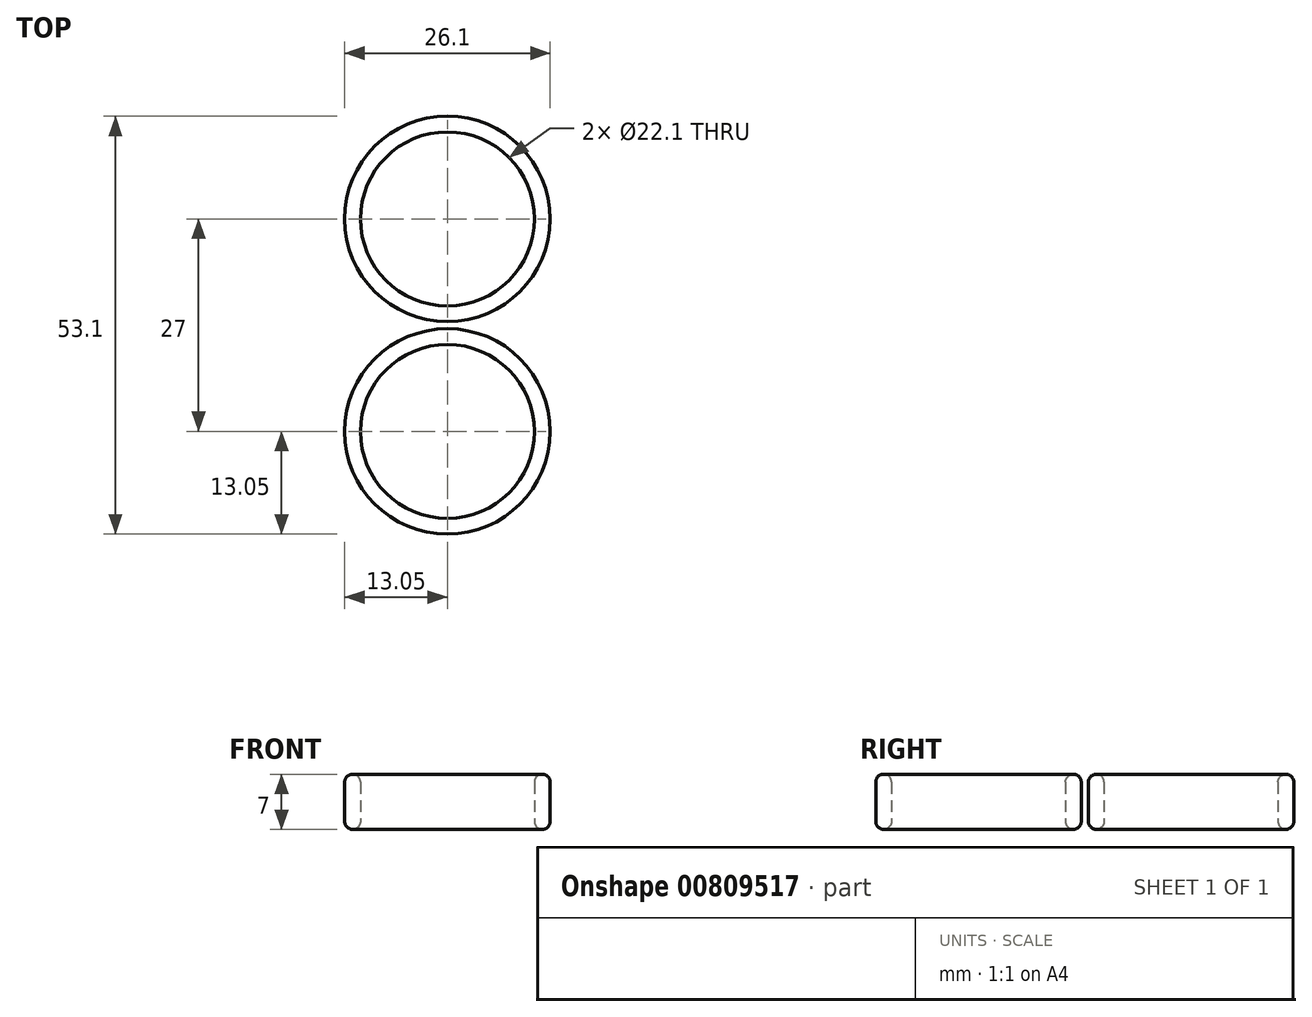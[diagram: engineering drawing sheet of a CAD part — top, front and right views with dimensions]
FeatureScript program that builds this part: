
annotation { "Feature Type Name" : "Feature", "Feature Type Description" : "" }
export const myFeature = defineFeature(function(context is Context, id is Id, definition is map)
    precondition{}
    {
        {
            var Q0;
            Q0=qCreatedBy(makeId("Top.planeOp"),FACE);
            var sketch = newSketch(context, id + "F0", { "sketchPlane" : qUnion([Q0])});
            skCircle(sketch, "E0", {"center": v(0, 0) * mm, "radius": 11.05 * mm});
            skCircle(sketch, "E1.0", {"center": v(0, 0) * mm, "radius": 13.05 * mm});
            skCircle(sketch, "E2", {"center": v(0, 27) * mm, "radius": 11.05 * mm});
            skCircle(sketch, "E3.0", {"center": v(0, 27) * mm, "radius": 13.05 * mm});
            skFitSpline(sketch, "E4", {"points": [v(12.68, 3.09) * mm, v(1.73, 13.5) * mm, v(12.68, 23.91) * mm], "startDerivative": vector(-13.43, 55.17) * mm, "endDerivative": vector(13.43, 55.17) * mm});
            skFitSpline(sketch, "E5", {"points": [v(-13.04, 27.4) * mm, v(-20.12, 13.5) * mm, v(-13.04, -0.4) * mm], "startDerivative": vector(-2.22, -73.4) * mm, "endDerivative": vector(2.22, -73.4) * mm});
            skLineSegment(sketch, "E6", {"start": v(0, 58.81) * mm, "end": v(0, -18.81) * mm, "construction": true});
            skLineSegment(sketch, "E7", {"start": v(-42.72, 13.5) * mm, "end": v(42.72, 13.5) * mm, "construction": true});
            skSolve(sketch);
        }
        {
            var Q0;
            Q0=makeQuery(id+"F0.imprint","IMPRINT",FACE,{"disambiguationData":[TD([[makeQuery(id+"F0.imprint","IMPRINT",EDGE,{"derivedFrom":sQuery(id+"F0.wireOp",EDGE,"E2")}),-1.0]])]});
            var Q1;
            {var subQ0=sQuery(id+"F0.wireOp",EDGE,"E4");Q1=makeQuery(id+"F0.imprint","IMPRINT",FACE,{"disambiguationData":[TD([[makeQuery(id+"F0.imprint","IMPRINT",EDGE,{"derivedFrom":subQ0}),1.0]])]});}
            var Q2;
            Q2=makeQuery(id+"F0.imprint","IMPRINT",FACE,{"disambiguationData":[TD([[makeQuery(id+"F0.imprint","IMPRINT",EDGE,{"derivedFrom":sQuery(id+"F0.wireOp",EDGE,"E0")}),-1.0]])]});
            extrude(context, id + "F1", {"entities" : qUnion([Q0, Q1, Q2]), "depth" : 7 * mm, "offsetDistance" : 25 * mm});
        }
        {
            var Q0;
            Q0=makeQuery(id+"F1.opExtrude","SWEPT_BODY",BODY,{"disambiguationData":[OSD([sQuery(id+"F0.wireOp",EDGE,"E0"),sQuery(id+"F0.wireOp",EDGE,"E1.0"),sQuery(id+"F0.wireOp",EDGE,"E2"),sQuery(id+"F0.wireOp",EDGE,"E3.0"),sQuery(id+"F0.wireOp",EDGE,"E4"),sQuery(id+"F0.wireOp",EDGE,"E5")])]});
            var Q1;
            Q1=makeQuery(id+"FXfsDHjoM9eOzzd_1.1.F1.opExtrude","SWEPT_BODY",BODY,{"disambiguationData":[OSD([sQuery(id+"F0.wireOp",EDGE,"E0"),sQuery(id+"F0.wireOp",EDGE,"E1.0"),sQuery(id+"F0.wireOp",EDGE,"E2"),sQuery(id+"F0.wireOp",EDGE,"E3.0"),sQuery(id+"F0.wireOp",EDGE,"E4"),sQuery(id+"F0.wireOp",EDGE,"E5")])]});
            var Q2;
            Q2=makeQuery(id+"FXfsDHjoM9eOzzd_1.2.F1.opExtrude","SWEPT_BODY",BODY,{"disambiguationData":[OSD([sQuery(id+"F0.wireOp",EDGE,"E0"),sQuery(id+"F0.wireOp",EDGE,"E1.0"),sQuery(id+"F0.wireOp",EDGE,"E2"),sQuery(id+"F0.wireOp",EDGE,"E3.0"),sQuery(id+"F0.wireOp",EDGE,"E4"),sQuery(id+"F0.wireOp",EDGE,"E5")])]});
            var Q3;
            Q3=makeQuery(id+"FXfsDHjoM9eOzzd_1.3.F1.opExtrude","SWEPT_BODY",BODY,{"disambiguationData":[OSD([sQuery(id+"F0.wireOp",EDGE,"E0"),sQuery(id+"F0.wireOp",EDGE,"E1.0"),sQuery(id+"F0.wireOp",EDGE,"E2"),sQuery(id+"F0.wireOp",EDGE,"E3.0"),sQuery(id+"F0.wireOp",EDGE,"E4"),sQuery(id+"F0.wireOp",EDGE,"E5")])]});
            booleanBodies(context, id + "F2", {"operationType" : BooleanOperationType.UNION, "tools" : qUnion([Q0, Q1, Q2, Q3])});
        }
        {
            var Q0;
            {var subQ0=sQuery(id+"F0.wireOp",EDGE,"E5");var subQ1=sQuery(id+"F0.wireOp",EDGE,"E4");var subQ2=sQuery(id+"F0.wireOp",EDGE,"E3.0");var subQ3=sQuery(id+"F0.wireOp",EDGE,"E2");var subQ4=sQuery(id+"F0.wireOp",EDGE,"E1.0");var subQ5=sQuery(id+"F0.wireOp",EDGE,"E0");Q0=makeQuery(id+"F2.opBoolean","MERGE",FACE,{"derivedFrom":[makeQuery(id+"F1.opExtrude","CAP_FACE",FACE,{"disambiguationData":[OSD([subQ5,subQ4,subQ3,subQ2,subQ1,subQ0])],"isStart":false}),makeQuery(id+"FXfsDHjoM9eOzzd_1.1.F1.opExtrude","CAP_FACE",FACE,{"disambiguationData":[OSD([subQ5,subQ4,subQ3,subQ2,subQ1,subQ0])],"isStart":false}),makeQuery(id+"FXfsDHjoM9eOzzd_1.2.F1.opExtrude","CAP_FACE",FACE,{"disambiguationData":[OSD([subQ5,subQ4,subQ3,subQ2,subQ1,subQ0])],"isStart":false}),makeQuery(id+"FXfsDHjoM9eOzzd_1.3.F1.opExtrude","CAP_FACE",FACE,{"disambiguationData":[OSD([subQ5,subQ4,subQ3,subQ2,subQ1,subQ0])],"isStart":false})]});}
            var Q1;
            {var subQ0=sQuery(id+"F0.wireOp",EDGE,"E5");var subQ1=sQuery(id+"F0.wireOp",EDGE,"E4");var subQ2=sQuery(id+"F0.wireOp",EDGE,"E3.0");var subQ3=sQuery(id+"F0.wireOp",EDGE,"E2");var subQ4=sQuery(id+"F0.wireOp",EDGE,"E1.0");var subQ5=sQuery(id+"F0.wireOp",EDGE,"E0");Q1=makeQuery(id+"F2.opBoolean","MERGE",FACE,{"derivedFrom":[makeQuery(id+"F1.opExtrude","CAP_FACE",FACE,{"disambiguationData":[OSD([subQ5,subQ4,subQ3,subQ2,subQ1,subQ0])],"isStart":true}),makeQuery(id+"FXfsDHjoM9eOzzd_1.1.F1.opExtrude","CAP_FACE",FACE,{"disambiguationData":[OSD([subQ5,subQ4,subQ3,subQ2,subQ1,subQ0])],"isStart":true}),makeQuery(id+"FXfsDHjoM9eOzzd_1.2.F1.opExtrude","CAP_FACE",FACE,{"disambiguationData":[OSD([subQ5,subQ4,subQ3,subQ2,subQ1,subQ0])],"isStart":true}),makeQuery(id+"FXfsDHjoM9eOzzd_1.3.F1.opExtrude","CAP_FACE",FACE,{"disambiguationData":[OSD([subQ5,subQ4,subQ3,subQ2,subQ1,subQ0])],"isStart":true})]});}
            fillet(context, id + "F3", {"entities" : qUnion([Q0, Q1]), "radius" : 1 * mm, "tangentPropagation" : true, "allowEdgeOverflow" : false});
        }
    });
